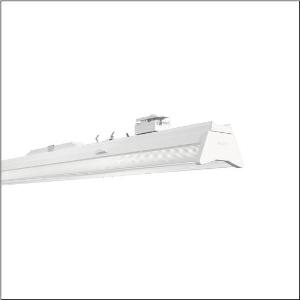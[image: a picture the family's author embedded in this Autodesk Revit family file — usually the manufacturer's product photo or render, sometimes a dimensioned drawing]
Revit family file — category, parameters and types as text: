
# Revit family: licross_r__11_performance_mo_51td167n485g_c044
name_source: partatom
category: Lighting Fixtures
units: mm (PartAtom-declared; Revit-internal decimal feet)

## family parameters
Cut with Voids When Loaded = No
Host = Face
Light Source = No
Part Type = Normal
Room Calculation Point = No
Round Connector Dimension = Use Diameter
Shared = No

## types (1)
- Licross® 11 Performance MO (1 x LED, 8840 lm, 48.6 W, 4000K)
    Apparent Load = 49 VA
    CIE Flux Codes = 66 88 96 79 100
    Color Rendering = 80
    Color Temperature = 4000K
    Default Elevation = 1800 mm
    Description = Licross® 11 Performance MO, luminaire insert, of sheet steel, galvanised, coil coated, white, length: 1.500mm, width: 120mm, height: 123mm, LED rated luminous flux: 8.840lm, light colour: 840, control gear: ON/OFF, with plug, 3-pole, with phase selection, mains connection: 220..240V, AC, 50/60Hz, rated input power: 49W, halogen-free wiring, primary light control with lens, of plastic, primary optical cover: cover, of PMMA, light emission: direct/indirect distribution, primary light characteristic: symmetric, protection rating (complete): IP54, insulation class (complete): insulation class I (protective earthing), certification: CE, ENEC, VDE, UKCA, protection symbol: D if used in an environment with non-conductive dust loads with corresponding accessories, impact resistance: IK06, permissible ambient temperature for indoor applications: -25..+35°C, corresponds to IFS (International Featured Standards) requirements for safety and quality in the food industry, reducing of maximum allowable ambient temperature of 5°C with ceiling mounting, LABS conformity tested according to VDMA 24364:2018-05, packaging unit: 1 piece
    Height = 114 mm
    Lamp = 1 x LED
    Lamp Light Flux = 8840 lm
    Lamp Power = 48.6 W
    Lamp count = 1
    Length = 1500 mm
    Luminous efficacy = 182 lm/W
    Manufacturer = Siteco
    ModVariant = No
    Model = 51TD167N485G
    Mounting Place = Ceiling
    Mounting Type = Pendant
    Number of Poles = 1
    OnlyDefault = Yes
    Power Factor = 1
    Product Name = Licross® 11 Performance MO
    Product group = luminaire insert
    ProductGroupID = 901
    Protection Class = Protection class I
    Protection Degree = IP 54
    RLX_Detail_Level = 1
    RLX_Emergency_Light_Flux = 0 lm
    RLX_Emergency_Type = 0
    RLX_Emergency_Type_DB = No
    RlxData = <blob elided: 30389 chars, md5=dfb5a219>
    Socket = socket
    Standby Power = 0 W
    System Light Flux = 8840 lm
    System Power = 49 W
    Type Comments = Product without accessories
    Type Image = l_1256138.jpg
    URL = http://relux.com
    VarID = ---
    Voltage = 0 V
    Weight = 0.00 kg
    Width = 120 mm

## geometry (parser evidence)
native form markers: Blend x4, Sweep x11
no freeform markers — native parametric forms only
